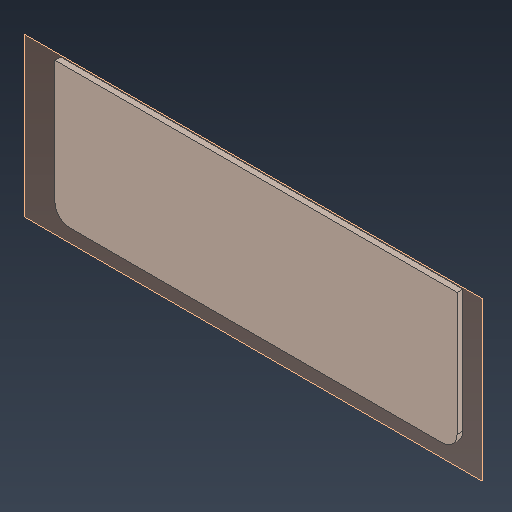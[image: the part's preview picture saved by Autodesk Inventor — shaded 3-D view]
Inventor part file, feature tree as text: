
AUTODESK INVENTOR PART (.ipt)
format: ipt  version: 2021 (Build 250183000, 183)  size: 97,280 bytes
history: native  units: mm
features: other x3, reference x2, plane x1, extrude x1, thicken_offset x1, sketch x1
ambient origin geometry x8: Origin, YZ Plane, XZ Plane, XY Plane, X Axis, Y Axis, Z Axis, Center Point
bodies: Solid1 (feature_tree)
feature tree (9):
  plane  "Work Plane1"
  extrude  "Extrusion1"  Depth=1.5mm
  thicken_offset  "Thicken1"
  sketch  "Sketch1"  dims[d0=1.5mm d1=0.0mm d2=0.1mm d3=0.1mm]
  reference  "Reference1"
  reference  "Reference2"
  parser-record x1  (decoder bookkeeping rows leaked as tree rows — omitted from the tree; the rows remain in map.json)
  other  "NEW_COVER_220DET_COMPLETE.iam"
  other  "NEW_COVER_220DET:1"
note: 1 file-system path scrubbed to <path> (originals preserved in map.json)
